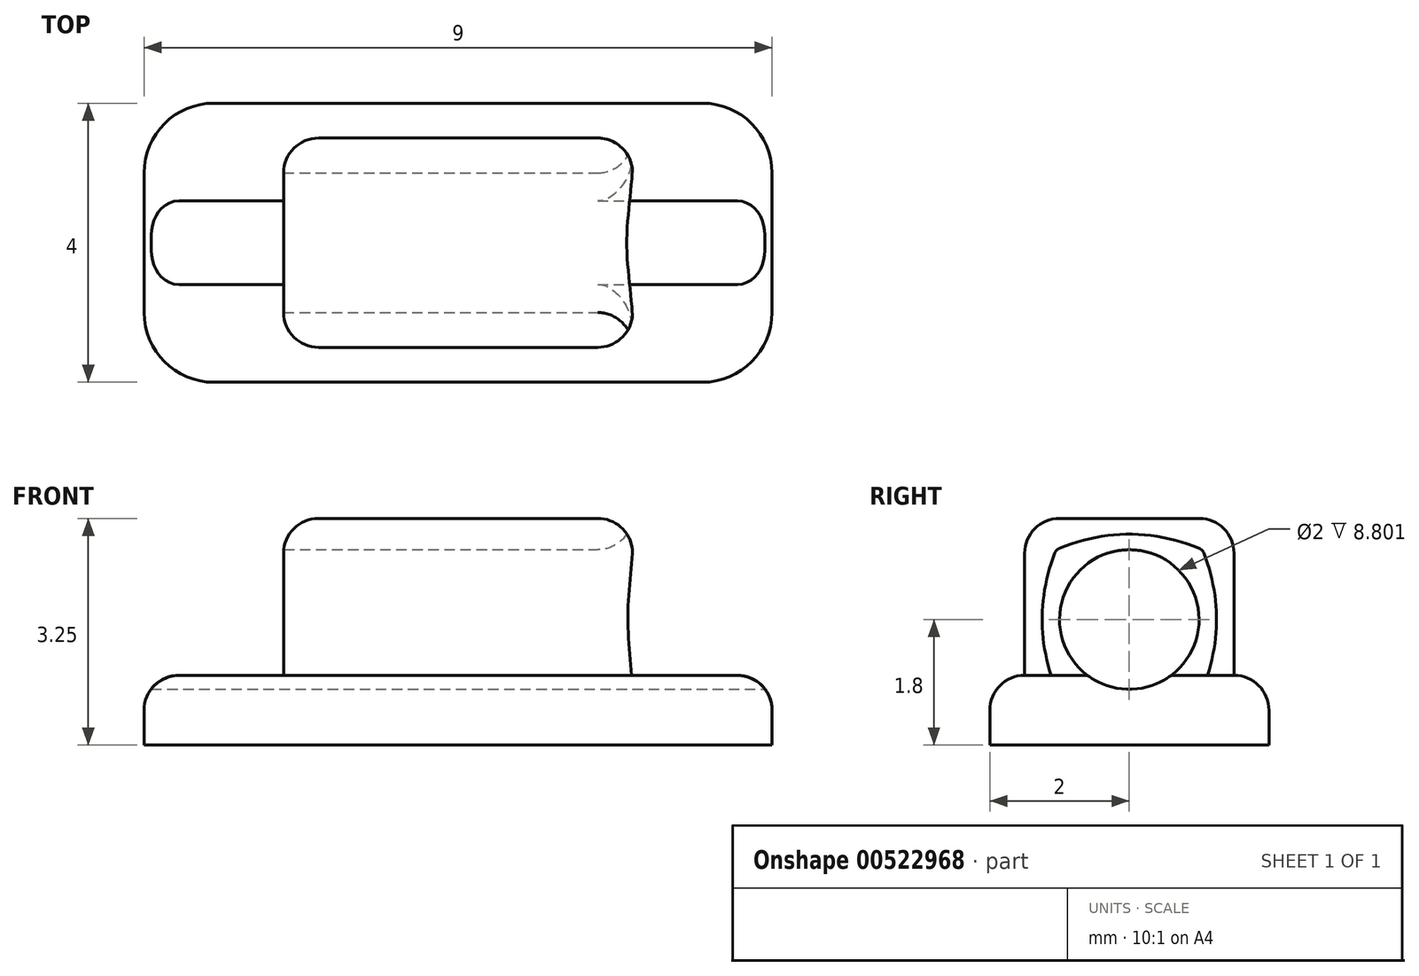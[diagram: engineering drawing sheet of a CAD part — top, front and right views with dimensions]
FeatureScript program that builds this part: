
annotation { "Feature Type Name" : "Feature", "Feature Type Description" : "" }
export const myFeature = defineFeature(function(context is Context, id is Id, definition is map)
    precondition{}
    {
        {
            var Q0;
            Q0=qCreatedBy(makeId("Top.planeOp"),FACE);
            var sketch = newSketch(context, id + "F0", { "sketchPlane" : qUnion([Q0])});
            skLineSegment(sketch, "E0.bottom", {"start": v(0, 0) * mm, "end": v(9, 0) * mm});
            skLineSegment(sketch, "E0.top", {"start": v(0, 4) * mm, "end": v(9, 4) * mm});
            skLineSegment(sketch, "E0.left", {"start": v(0, 0) * mm, "end": v(0, 4) * mm});
            skLineSegment(sketch, "E0.right", {"start": v(9, 0) * mm, "end": v(9, 4) * mm});
            skPoint(sketch, "E1.firstSnap0", {"position": v(9, 0.5) * mm});
            skLineSegment(sketch, "E1.bottom", {"start": v(2, 0.5) * mm, "end": v(7, 0.5) * mm});
            skLineSegment(sketch, "E1.top", {"start": v(2, 3.5) * mm, "end": v(7, 3.5) * mm});
            skLineSegment(sketch, "E1.left", {"start": v(2, 0.5) * mm, "end": v(2, 3.5) * mm});
            skLineSegment(sketch, "E1.right", {"start": v(7, 0.5) * mm, "end": v(7, 3.5) * mm});
            skSolve(sketch);
        }
        {
            var Q0;
            Q0=makeQuery(id+"F0.imprint","IMPRINT",FACE,{"disambiguationData":[TD([[makeQuery(id+"F0.imprint","IMPRINT",EDGE,{"derivedFrom":sQuery(id+"F0.wireOp",EDGE,"E1.bottom")}),1.0]])]});
            var Q1;
            Q1 = qSketchRegion(id + "F3", true);
            extrude(context, id + "F1", {"entities" : qUnion([Q0, Q1]), "depth" : 3.25 * mm, "offsetDistance" : 25 * mm});
        }
        {
            var Q0;
            Q0 = qSketchRegion(id + "F0", true);
            extrude(context, id + "F2", {"entities" : qUnion([Q0]), "operationType" : NewBodyOperationType.ADD, "depth" : 1 * mm, "offsetDistance" : 25 * mm});
        }
        {
            var Q0;
            Q0=makeQuery(id+"F1.opExtrude","SWEPT_FACE",FACE,{"disambiguationData":[OSD([sQuery(id+"F0.wireOp",EDGE,"E1.right")])]});
            var sketch = newSketch(context, id + "F3", { "sketchPlane" : qUnion([Q0])});
            skSolve(sketch);
        }
        {
            var Q0;
            {var subQ0=sQuery(id+"F0.wireOp",EDGE,"E1.right");Q0=makeQuery(id+"F3.imprint","IMPRINT",FACE,{"disambiguationData":[TD([[makeQuery(id+"F3.imprint","IMPRINT",EDGE,{"derivedFrom":makeQuery(id+"F1.opExtrude","CAP_EDGE",EDGE,{"disambiguationData":[OSD([subQ0])],"isStart":false})}),-1.0]])]});}
            var sketch = newSketch(context, id + "F4", { "sketchPlane" : qUnion([Q0])});
            skCircle(sketch, "E2", {"center": v(2, 1.8) * mm, "radius": 1 * mm});
            skSolve(sketch);
        }
        {
            var Q0;
            Q0=makeQuery(id+"F4.imprint","IMPRINT",FACE,{"disambiguationData":[TD([[makeQuery(id+"F4.imprint","IMPRINT",EDGE,{"derivedFrom":sQuery(id+"F4.wireOp",EDGE,"E2")}),1.0]])]});
            var Q1;
            Q1=sQuery(id+"F4.wireOp",EDGE,"E2");
            extrude(context, id + "F5", {"entities" : qUnion([Q0]), "operationType" : NewBodyOperationType.REMOVE, "surfaceEntities" : qUnion([Q1]), "endBound" : BoundingType.SYMMETRIC, "oppositeDirection" : true, "depth" : 25 * mm, "offsetDistance" : 25 * mm});
        }
        {
            var Q0;
            Q0=makeQuery(id+"F1.opExtrude","CAP_EDGE",EDGE,{"disambiguationData":[OSD([sQuery(id+"F0.wireOp",EDGE,"E1.bottom")])],"isStart":false});
            var Q1;
            Q1=makeQuery(id+"F1.opExtrude","CAP_EDGE",EDGE,{"disambiguationData":[OSD([sQuery(id+"F0.wireOp",EDGE,"E1.top")])],"isStart":false});
            var Q2;
            Q2=makeQuery(id+"F1.opExtrude","CAP_EDGE",EDGE,{"disambiguationData":[OSD([sQuery(id+"F0.wireOp",EDGE,"E1.right")])],"isStart":false});
            var Q3;
            Q3=makeQuery(id+"F1.opExtrude","CAP_EDGE",EDGE,{"disambiguationData":[OSD([sQuery(id+"F0.wireOp",EDGE,"E1.left")])],"isStart":false});
            var Q4;
            Q4=makeQuery(id+"F1.opExtrude","SWEPT_EDGE",EDGE,{"disambiguationData":[OSD([sQuery(id+"F0.wireOp",EDGE,"E1.bottom"),sQuery(id+"F0.wireOp",EDGE,"E1.right")])]});
            var Q5;
            Q5=makeQuery(id+"F1.opExtrude","SWEPT_EDGE",EDGE,{"disambiguationData":[OSD([sQuery(id+"F0.wireOp",EDGE,"E1.top"),sQuery(id+"F0.wireOp",EDGE,"E1.right")])]});
            var Q6;
            Q6=makeQuery(id+"F5.boolean.opBoolean","INTERSECT",EDGE,{"derivedFrom":[makeQuery(id+"F1.opExtrude","SWEPT_FACE",FACE,{"disambiguationData":[OSD([sQuery(id+"F0.wireOp",EDGE,"E1.right")])]}),makeQuery(id+"F5.opExtrude","SWEPT_FACE",FACE,{"disambiguationData":[OSD([sQuery(id+"F4.wireOp",EDGE,"E2")])]})]});
            var Q7;
            Q7=makeQuery(id+"F1.opExtrude","SWEPT_EDGE",EDGE,{"disambiguationData":[OSD([sQuery(id+"F0.wireOp",EDGE,"E1.bottom"),sQuery(id+"F0.wireOp",EDGE,"E1.left")])]});
            var Q8;
            Q8=makeQuery(id+"F1.opExtrude","SWEPT_EDGE",EDGE,{"disambiguationData":[OSD([sQuery(id+"F0.wireOp",EDGE,"E1.top"),sQuery(id+"F0.wireOp",EDGE,"E1.left")])]});
            fillet(context, id + "F6", {"entities" : qUnion([Q0, Q1, Q2, Q3, Q4, Q5, Q6, Q7, Q8]), "radius" : 0.5 * mm, "tangentPropagation" : true, "allowEdgeOverflow" : false});
        }
        {
            var Q0;
            Q0=makeQuery(id+"F2.opExtrude","CAP_EDGE",EDGE,{"disambiguationData":[OSD([sQuery(id+"F0.wireOp",EDGE,"E0.top")])],"isStart":false});
            var Q1;
            Q1=makeQuery(id+"F2.opExtrude","CAP_EDGE",EDGE,{"disambiguationData":[OSD([sQuery(id+"F0.wireOp",EDGE,"E0.bottom")])],"isStart":false});
            var Q2;
            {var subQ0=sQuery(id+"F0.wireOp",EDGE,"E0.bottom");var subQ1=sQuery(id+"F0.wireOp",EDGE,"E0.left");Q2=makeQuery(id+"F5.boolean.opBoolean","SPLIT",EDGE,{"disambiguationData":[TD([makeQuery(id+"F2.opExtrude","SWEPT_FACE",FACE,{"disambiguationData":[OSD([subQ0])]})])],"derivedFrom":makeQuery(id+"F2.opExtrude","CAP_EDGE",EDGE,{"disambiguationData":[OSD([subQ1])],"isStart":false})});}
            var Q3;
            {var subQ0=sQuery(id+"F0.wireOp",EDGE,"E0.right");var subQ1=sQuery(id+"F0.wireOp",EDGE,"E0.top");Q3=makeQuery(id+"F5.boolean.opBoolean","SPLIT",EDGE,{"disambiguationData":[TD([makeQuery(id+"F2.opExtrude","SWEPT_FACE",FACE,{"disambiguationData":[OSD([subQ1])]})])],"derivedFrom":makeQuery(id+"F2.opExtrude","CAP_EDGE",EDGE,{"disambiguationData":[OSD([subQ0])],"isStart":false})});}
            fillet(context, id + "F7", {"entities" : qUnion([Q0, Q1, Q2, Q3]), "radius" : 0.5 * mm, "tangentPropagation" : true, "allowEdgeOverflow" : false});
        }
        {
            var Q0;
            Q0=makeQuery(id+"F2.opExtrude","SWEPT_EDGE",EDGE,{"disambiguationData":[OSD([sQuery(id+"F0.wireOp",EDGE,"E0.bottom"),sQuery(id+"F0.wireOp",EDGE,"E0.right")])]});
            var Q1;
            Q1=makeQuery(id+"F2.opExtrude","SWEPT_EDGE",EDGE,{"disambiguationData":[OSD([sQuery(id+"F0.wireOp",EDGE,"E0.top"),sQuery(id+"F0.wireOp",EDGE,"E0.right")])]});
            var Q2;
            Q2=makeQuery(id+"F2.opExtrude","SWEPT_EDGE",EDGE,{"disambiguationData":[OSD([sQuery(id+"F0.wireOp",EDGE,"E0.bottom"),sQuery(id+"F0.wireOp",EDGE,"E0.left")])]});
            var Q3;
            Q3=makeQuery(id+"F2.opExtrude","SWEPT_EDGE",EDGE,{"disambiguationData":[OSD([sQuery(id+"F0.wireOp",EDGE,"E0.top"),sQuery(id+"F0.wireOp",EDGE,"E0.left")])]});
            fillet(context, id + "F8", {"entities" : qUnion([Q0, Q1, Q2, Q3]), "radius" : 1 * mm, "tangentPropagation" : true, "allowEdgeOverflow" : false});
        }
    });
